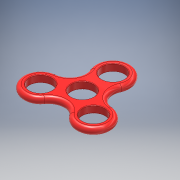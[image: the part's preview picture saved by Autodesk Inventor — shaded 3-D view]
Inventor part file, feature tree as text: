
AUTODESK INVENTOR PART (.ipt)
format: ipt  version: 2018 (Build 220112000, 112)  size: 210,432 bytes
history: native  units: mm
features: fillet x2, extrude x1, sketch x1
ambient origin geometry x8: Origin, YZ Plane, XZ Plane, XY Plane, X Axis, Y Axis, Z Axis, Center Point
bodies: Solid1 (feature_tree)
feature tree (4):
  extrude  "Extrusion1"  Depth=0.5mm
  fillet  "Fillet1"  Radius=30.0mm
  fillet  "Fillet2"  Radius=30.0mm
  sketch  "Sketch1"  dims[d0=22.0mm d1=22.0mm d2=30.0mm d3=30.0mm d5=360.0deg d7=6.0mm d8=6.0mm d9=6.0mm d10=15.0mm d11=15.0mm d12=15.0mm d13=7.0mm d14=0.0mm d15=0.5mm]
